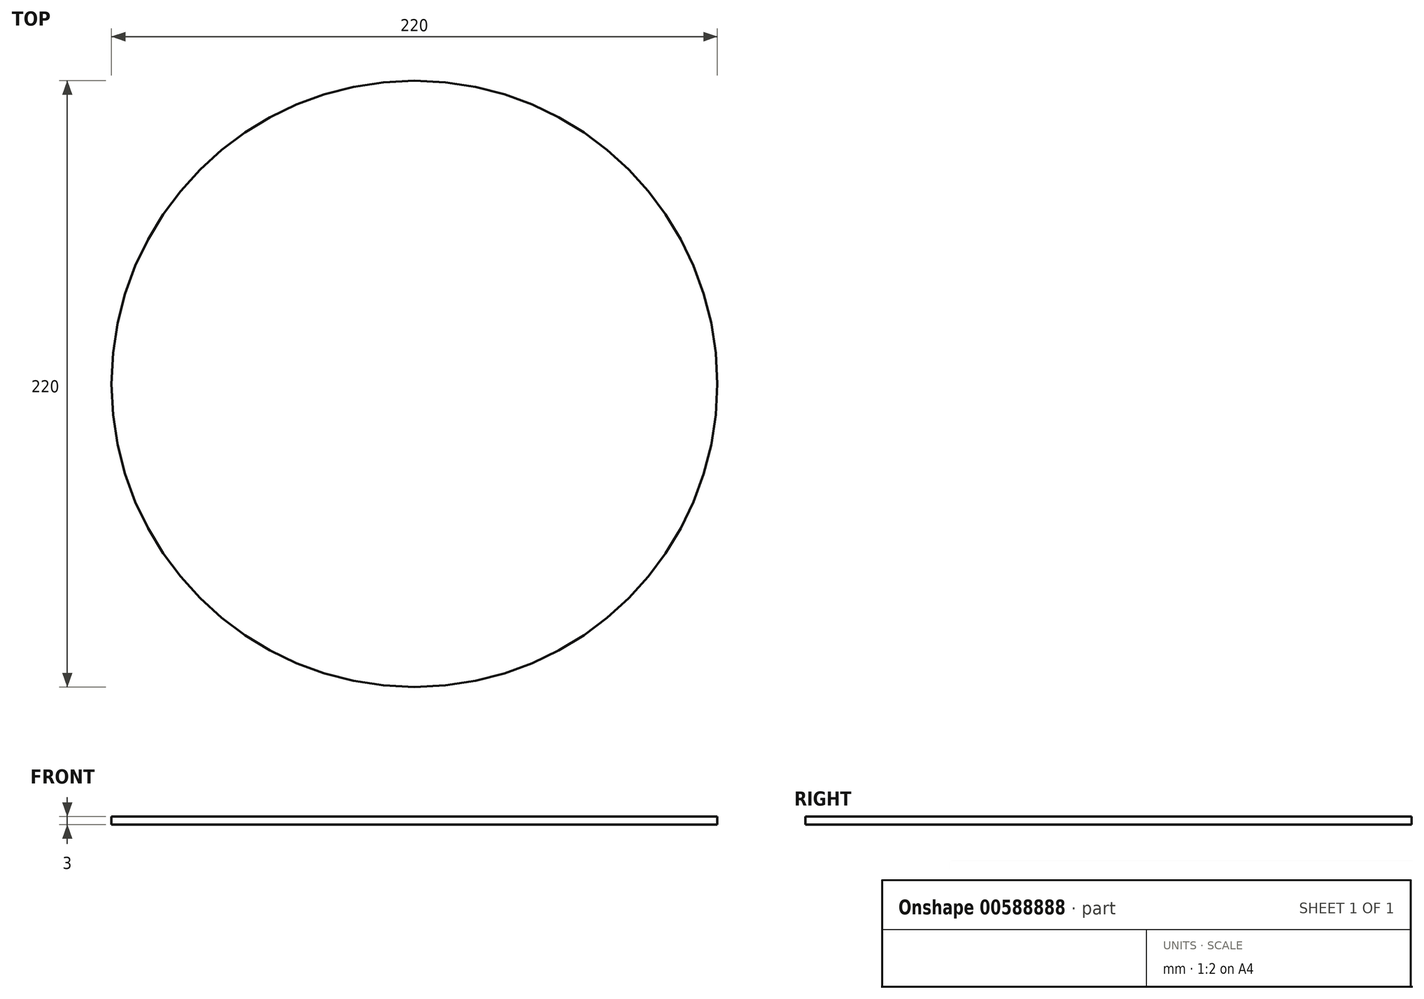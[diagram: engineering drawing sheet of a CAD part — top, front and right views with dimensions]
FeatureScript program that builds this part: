
annotation { "Feature Type Name" : "Feature", "Feature Type Description" : "" }
export const myFeature = defineFeature(function(context is Context, id is Id, definition is map)
    precondition{}
    {
        {
            var Q0;
            Q0=qCreatedBy(makeId("Top.planeOp"),FACE);
            var sketch = newSketch(context, id + "F0", { "sketchPlane" : qUnion([Q0])});
            skCircle(sketch, "E0", {"center": v(0, 0) * mm, "radius": 110 * mm});
            skSolve(sketch);
        }
        {
            var Q0;
            Q0=makeQuery(id+"F0.imprint","IMPRINT",FACE,{"disambiguationData":[TD([[makeQuery(id+"F0.imprint","IMPRINT",EDGE,{"derivedFrom":sQuery(id+"F0.wireOp",EDGE,"E0")}),1.0]])]});
            extrude(context, id + "F1", {"entities" : qUnion([Q0]), "depth" : 3 * mm, "offsetDistance" : 25 * mm});
        }
    });
